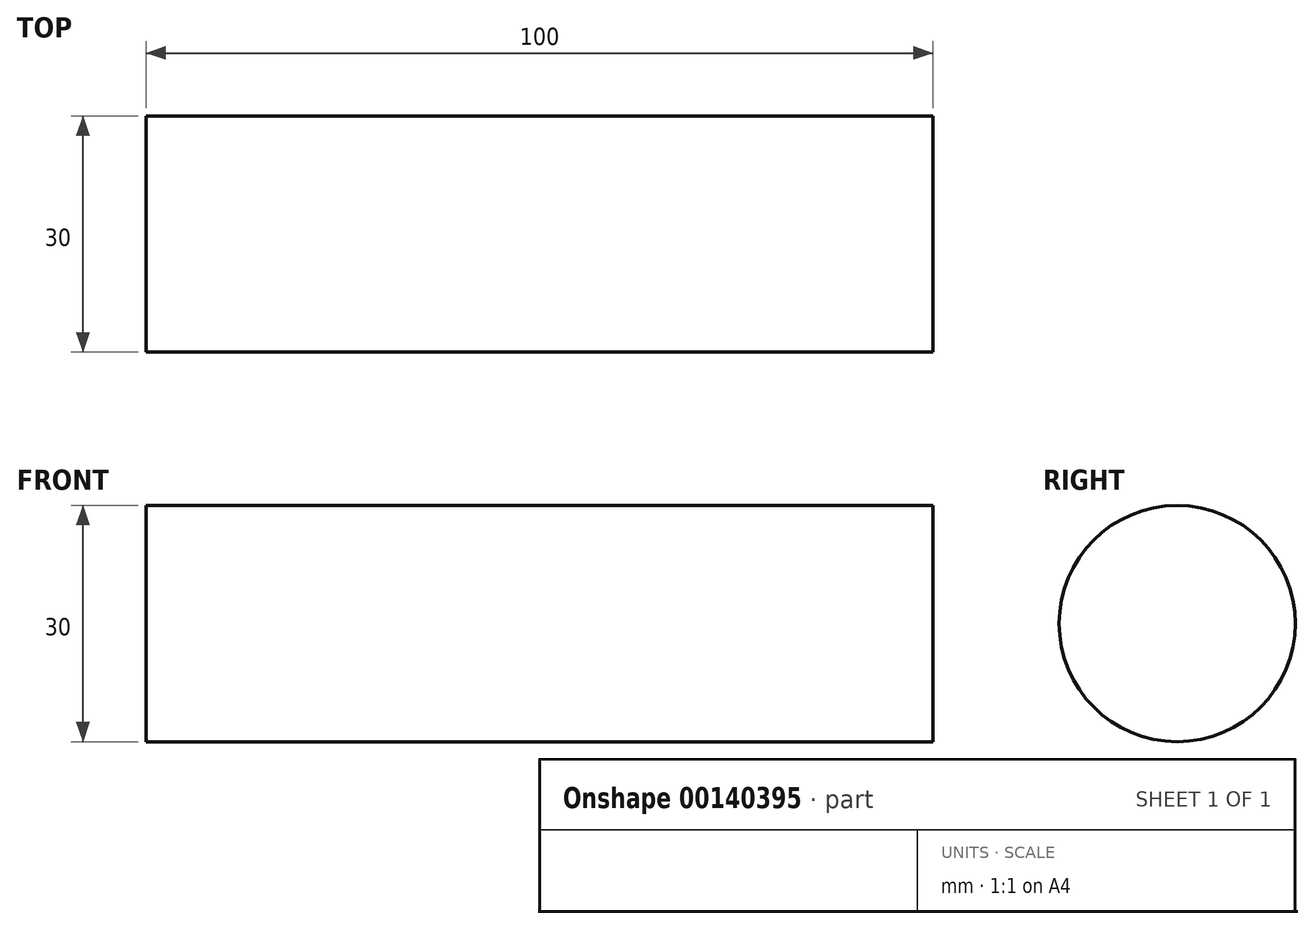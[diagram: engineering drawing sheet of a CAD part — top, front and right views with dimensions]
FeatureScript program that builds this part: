
annotation { "Feature Type Name" : "Feature", "Feature Type Description" : "" }
export const myFeature = defineFeature(function(context is Context, id is Id, definition is map)
    precondition{}
    {
        {
            var Q0;
            Q0=qCreatedBy(makeId("Top.planeOp"),FACE);
            var sketch = newSketch(context, id + "F0", { "sketchPlane" : qUnion([Q0])});
            skLineSegment(sketch, "E0.bottom", {"start": v(-50, 15) * mm, "end": v(50, 15) * mm});
            skLineSegment(sketch, "E0.top", {"start": v(-50, 0) * mm, "end": v(50, 0) * mm});
            skLineSegment(sketch, "E0.left", {"start": v(-50, 15) * mm, "end": v(-50, 0) * mm});
            skLineSegment(sketch, "E0.right", {"start": v(50, 15) * mm, "end": v(50, 0) * mm});
            skLineSegment(sketch, "E1", {"start": v(-50, 0) * mm, "end": v(69.72, 0) * mm, "construction": true});
            skSolve(sketch);
        }
        {
            var Q0;
            Q0=makeQuery(id+"F0.imprint","IMPRINT",FACE,{"disambiguationData":[TD([[makeQuery(id+"F0.imprint","IMPRINT",EDGE,{"derivedFrom":sQuery(id+"F0.wireOp",EDGE,"E0.bottom")}),-1.0]])]});
            var Q1;
            Q1=sQuery(id+"F0.wireOp",EDGE,"E0.top");
            revolve(context, id + "F1", {"entities" : qUnion([Q0]), "axis" : qUnion([Q1]), "revolveType" : RevolveType.FULL});
        }
    });
